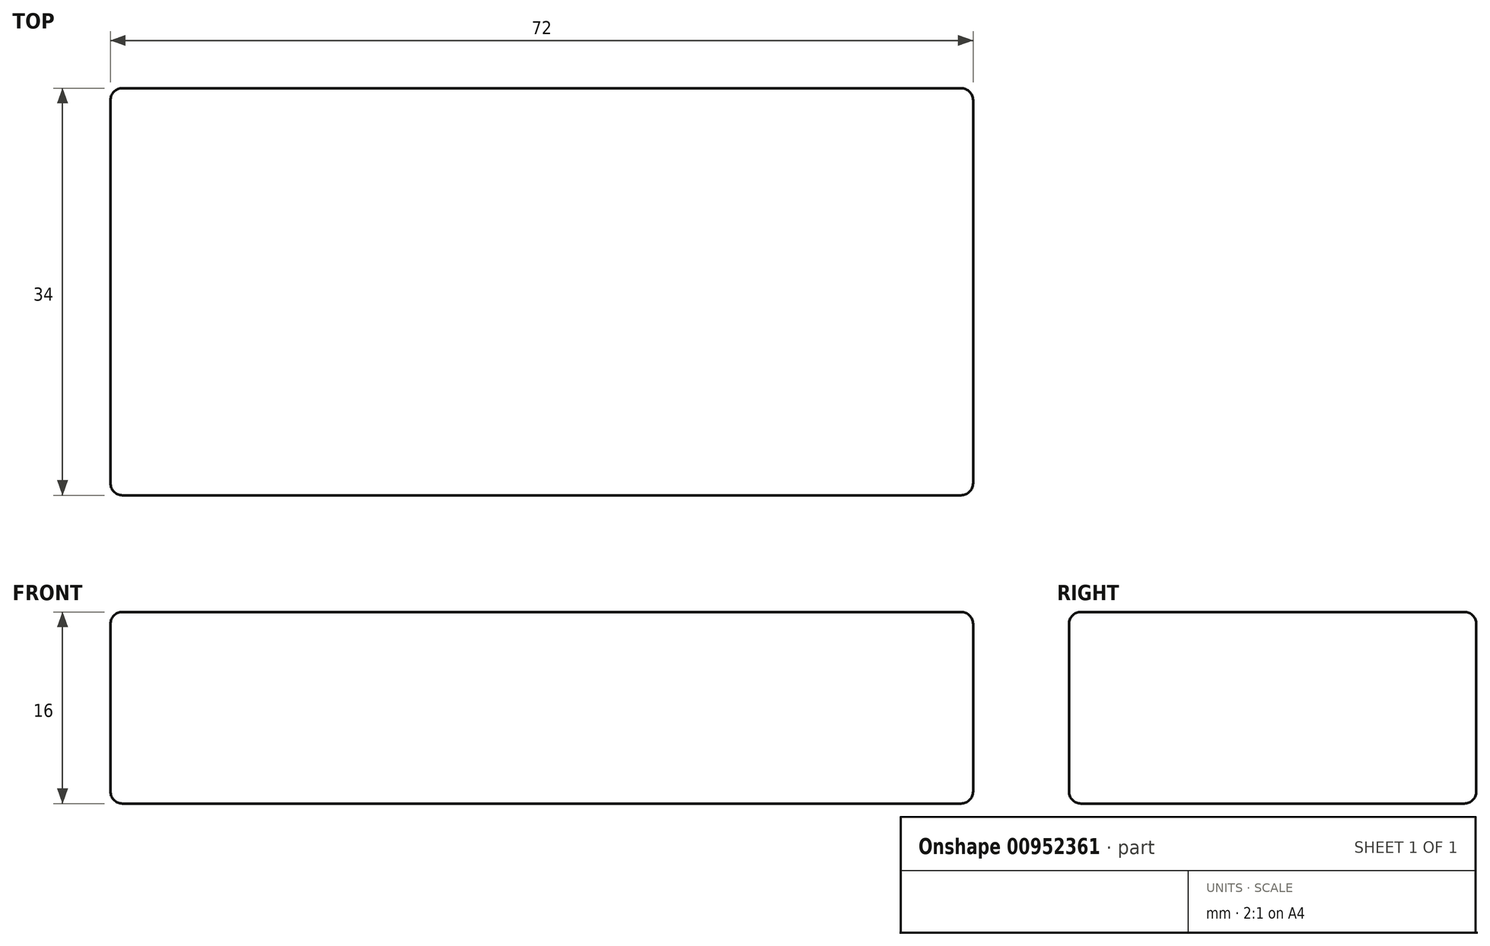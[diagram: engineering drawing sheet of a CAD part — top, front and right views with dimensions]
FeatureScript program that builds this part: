
annotation { "Feature Type Name" : "Feature", "Feature Type Description" : "" }
export const myFeature = defineFeature(function(context is Context, id is Id, definition is map)
    precondition{}
    {
        {
            var Q0;
            Q0=qCreatedBy(makeId("Top.planeOp"),FACE);
            var sketch = newSketch(context, id + "F0", { "sketchPlane" : qUnion([Q0])});
            skLineSegment(sketch, "E0.bottom", {"start": v(36, 17) * mm, "end": v(-36, 17) * mm});
            skLineSegment(sketch, "E0.top", {"start": v(36, -17) * mm, "end": v(-36, -17) * mm});
            skLineSegment(sketch, "E0.left", {"start": v(36, 17) * mm, "end": v(36, -17) * mm});
            skLineSegment(sketch, "E0.right", {"start": v(-36, 17) * mm, "end": v(-36, -17) * mm});
            skPoint(sketch, "E0.middle", {"position": v(0, 0) * mm});
            skSolve(sketch);
        }
        {
            var Q0;
            Q0=makeQuery(id+"F0.imprint","IMPRINT",FACE,{"disambiguationData":[TD([[makeQuery(id+"F0.imprint","IMPRINT",EDGE,{"derivedFrom":sQuery(id+"F0.wireOp",EDGE,"E0.bottom")}),1.0]])]});
            extrude(context, id + "F1", {"entities" : qUnion([Q0]), "depth" : 16 * mm, "offsetDistance" : 25 * mm});
        }
        {
            var Q0;
            Q0=makeQuery(id+"F1.opExtrude","CAP_EDGE",EDGE,{"disambiguationData":[OSD([sQuery(id+"F0.wireOp",EDGE,"E0.right")])],"isStart":false});
            var Q1;
            Q1=makeQuery(id+"F1.opExtrude","CAP_EDGE",EDGE,{"disambiguationData":[OSD([sQuery(id+"F0.wireOp",EDGE,"E0.top")])],"isStart":false});
            var Q2;
            Q2=makeQuery(id+"F1.opExtrude","SWEPT_EDGE",EDGE,{"disambiguationData":[OSD([sQuery(id+"F0.wireOp",EDGE,"E0.top"),sQuery(id+"F0.wireOp",EDGE,"E0.right")])]});
            var Q3;
            Q3=makeQuery(id+"F1.opExtrude","CAP_EDGE",EDGE,{"disambiguationData":[OSD([sQuery(id+"F0.wireOp",EDGE,"E0.right")])],"isStart":true});
            var Q4;
            Q4=makeQuery(id+"F1.opExtrude","CAP_EDGE",EDGE,{"disambiguationData":[OSD([sQuery(id+"F0.wireOp",EDGE,"E0.top")])],"isStart":true});
            var Q5;
            Q5=makeQuery(id+"F1.opExtrude","SWEPT_EDGE",EDGE,{"disambiguationData":[OSD([sQuery(id+"F0.wireOp",EDGE,"E0.top"),sQuery(id+"F0.wireOp",EDGE,"E0.left")])]});
            var Q6;
            Q6=makeQuery(id+"F1.opExtrude","CAP_EDGE",EDGE,{"disambiguationData":[OSD([sQuery(id+"F0.wireOp",EDGE,"E0.left")])],"isStart":false});
            var Q7;
            Q7=makeQuery(id+"F1.opExtrude","CAP_EDGE",EDGE,{"disambiguationData":[OSD([sQuery(id+"F0.wireOp",EDGE,"E0.left")])],"isStart":true});
            var Q8;
            Q8=makeQuery(id+"F1.opExtrude","SWEPT_EDGE",EDGE,{"disambiguationData":[OSD([sQuery(id+"F0.wireOp",EDGE,"E0.bottom"),sQuery(id+"F0.wireOp",EDGE,"E0.left")])]});
            var Q9;
            Q9=makeQuery(id+"F1.opExtrude","CAP_EDGE",EDGE,{"disambiguationData":[OSD([sQuery(id+"F0.wireOp",EDGE,"E0.bottom")])],"isStart":false});
            var Q10;
            Q10=makeQuery(id+"F1.opExtrude","CAP_EDGE",EDGE,{"disambiguationData":[OSD([sQuery(id+"F0.wireOp",EDGE,"E0.bottom")])],"isStart":true});
            var Q11;
            Q11=makeQuery(id+"F1.opExtrude","SWEPT_EDGE",EDGE,{"disambiguationData":[OSD([sQuery(id+"F0.wireOp",EDGE,"E0.bottom"),sQuery(id+"F0.wireOp",EDGE,"E0.right")])]});
            fillet(context, id + "F2", {"entities" : qUnion([Q0, Q1, Q2, Q3, Q4, Q5, Q6, Q7, Q8, Q9, Q10, Q11]), "radius" : 1 * mm, "tangentPropagation" : true, "allowEdgeOverflow" : false});
        }
    });
